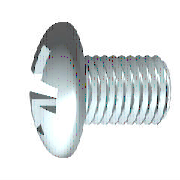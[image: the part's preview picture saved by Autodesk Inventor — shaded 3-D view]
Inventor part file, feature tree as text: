
AUTODESK INVENTOR PART (.ipt)
format: ipt  version: 2019 (Build 230136000, 136)  size: 269,312 bytes
history: native  units: mm (DEFAULTED — no unit token found)
features: extrude x1, other x1, plane x1
ambient origin geometry x7: Origin, YZ Plane, XZ Plane, X Axis, Y Axis, Z Axis, Center Point
bodies: Solid1 (feature_tree), Body (feature_tree)
feature tree (3):
  extrude  "Slot"  Depth=4.0mm
  other  "Cut"
  plane  "Work Plane3"
